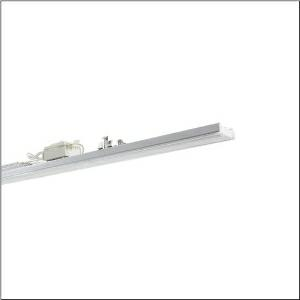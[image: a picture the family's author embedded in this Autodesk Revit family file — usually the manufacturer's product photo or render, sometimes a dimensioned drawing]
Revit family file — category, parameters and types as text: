
# Revit family: licross_r__21_recessed_mo_52tl12mn4a5g_9149
name_source: partatom
category: Lighting Fixtures
units: mm (PartAtom-declared; Revit-internal decimal feet)

## family parameters
Cut with Voids When Loaded = No
Host = Face
Light Source = No
Part Type = Normal
Room Calculation Point = No
Round Connector Dimension = Use Diameter
Shared = No

## types (1)
- --- (1 x LED, 10990 lm, 60.5 W, 4000K)
    Apparent Load = 61 VA
    CIE Flux Codes = 72 92 99 100 100
    Color Rendering = 80
    Color Temperature = 4000K
    Default Elevation = 1800 mm
    Description = Licross® 21 Recessed MO, luminaire insert, of sheet steel, galvanised, coil coated, white, length: 1.500mm, width: 66mm, height: 67mm, LED rated luminous flux: 10.990lm, light colour: 840, control gear: ON/OFF Multilumen, with plug, 3-pole, with phase selection, mains connection: 220..240V, AC, 50/60Hz, rated input power: 61W, halogen-free wiring, primary optical cover: cover, of PMMA, light emission: direct distribution, primary light characteristic: symmetric, protection rating (complete): IP40, insulation class (complete): insulation class I (protective earthing), certification: CE, ENEC, VDE, UKCA, protection symbol: D if used in an environment without relevant dust loads with corresponding accessories, impact resistance: IK06, permissible ambient temperature for indoor applications: -35..+40°C, corresponds to IFS (International Featured Standards) requirements for safety and quality in the food industry, reducing of maximum allowable ambient temperature of 5°C with ceiling mounting, LABS conformity tested according to VDMA 24364:2018-05, packaging unit: 1 piece
    Height = 58 mm
    Lamp = 1 x LED
    Lamp Light Flux = 10990 lm
    Lamp Power = 60.5 W
    Lamp count = 1
    Length = 1500 mm
    Luminous efficacy = 182 lm/W
    Manufacturer = Siteco
    ModVariant = No
    Model = 52TL12MN4A5G
    Mounting Place = Ceiling
    Mounting Type = Pendant
    Number of Poles = 1
    OnlyDefault = Yes
    Power Factor = 1
    Product Name = Licross® 21 Recessed MO
    Product group = luminaire insert
    ProductGroupID = 902
    Protection Class = Protection class I
    Protection Degree = IP 40
    RLX_Detail_Level = 1
    RLX_Emergency_Light_Flux = 0 lm
    RLX_Emergency_Type = 0
    RLX_Emergency_Type_DB = No
    RlxData = <blob elided: 22257 chars, md5=b1399d57>
    Socket = socket
    Standby Power = 0 W
    System Light Flux = 10990 lm
    System Power = 61 W
    Type Comments = factory setting: luminous flux: 100 % | (A | C | E) | 140 mA
    Type Image = l_1296930.jpg
    URL = http://relux.com
    VarID = @adj_108018
    Voltage = 0 V
    Weight = 0.00 kg
    Width = 66 mm

## geometry (parser evidence)
native form markers: Blend x4, Sweep x11
no freeform markers — native parametric forms only
